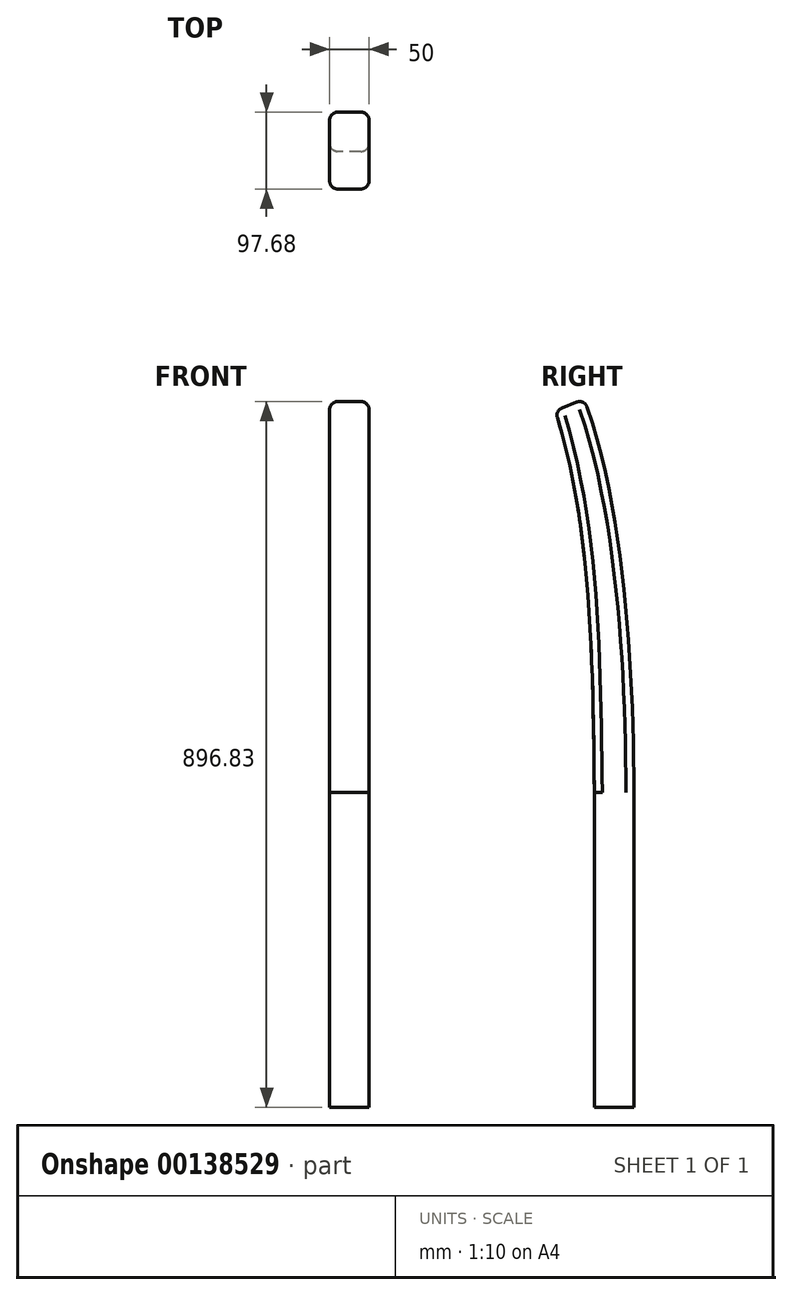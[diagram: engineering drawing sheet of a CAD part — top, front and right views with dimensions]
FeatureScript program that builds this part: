
annotation { "Feature Type Name" : "Feature", "Feature Type Description" : "" }
export const myFeature = defineFeature(function(context is Context, id is Id, definition is map)
    precondition{}
    {
        {
            var Q0;
            Q0=qCreatedBy(makeId("Right.planeOp"),FACE);
            var sketch = newSketch(context, id + "F0", { "sketchPlane" : qUnion([Q0])});
            skLineSegment(sketch, "E0.bottom", {"start": v(0, -400) * mm, "end": v(-100, -400) * mm, "construction": true});
            skLineSegment(sketch, "E0.top", {"start": v(0, 500) * mm, "end": v(-100, 500) * mm, "construction": true});
            skLineSegment(sketch, "E0.left", {"start": v(0, -400) * mm, "end": v(0, 500) * mm, "construction": true});
            skLineSegment(sketch, "E0.right", {"start": v(-100, -400) * mm, "end": v(-100, 500) * mm, "construction": true});
            skLineSegment(sketch, "E1", {"start": v(-50, -400) * mm, "end": v(-50, 0) * mm});
            skFitSpline(sketch, "E2", {"points": [v(0, 0) * mm, v(-62.92, 500) * mm], "startDerivative": vector(0, 501.4) * mm, "endDerivative": vector(-147.21, 397.99) * mm});
            skLineSegment(sketch, "E3", {"start": v(-62.92, 500) * mm, "end": v(-100, 485) * mm});
            skFitSpline(sketch, "E4", {"points": [v(-50, 0) * mm, v(-100, 485) * mm], "startDerivative": vector(-6.13, 505.96) * mm, "endDerivative": vector(-139.6, 432.37) * mm});
            skLineSegment(sketch, "E5", {"start": v(0, 0) * mm, "end": v(0, -400) * mm});
            skLineSegment(sketch, "E6", {"start": v(-50, -400) * mm, "end": v(0, -400) * mm});
            skSolve(sketch);
        }
        {
            var Q0;
            Q0=makeQuery(id+"F0.imprint","IMPRINT",FACE,{"disambiguationData":[TD([[makeQuery(id+"F0.imprint","IMPRINT",EDGE,{"derivedFrom":sQuery(id+"F0.wireOp",EDGE,"E1")}),-1.0]])]});
            extrude(context, id + "F1", {"entities" : qUnion([Q0]), "endBound" : BoundingType.SYMMETRIC, "depth" : 50 * mm});
        }
        {
            var Q0;
            Q0=makeQuery(id+"F1.opExtrude","CAP_EDGE",EDGE,{"disambiguationData":[OSD([sQuery(id+"F0.wireOp",EDGE,"E2")])],"isStart":false});
            var Q1;
            Q1=makeQuery(id+"F1.opExtrude","CAP_EDGE",EDGE,{"disambiguationData":[OSD([sQuery(id+"F0.wireOp",EDGE,"E4")])],"isStart":false});
            var Q2;
            Q2=makeQuery(id+"F1.opExtrude","CAP_EDGE",EDGE,{"disambiguationData":[OSD([sQuery(id+"F0.wireOp",EDGE,"E4")])],"isStart":true});
            var Q3;
            Q3=makeQuery(id+"F1.opExtrude","CAP_EDGE",EDGE,{"disambiguationData":[OSD([sQuery(id+"F0.wireOp",EDGE,"E2")])],"isStart":true});
            var Q4;
            Q4=makeQuery(id+"F1.opExtrude","CAP_EDGE",EDGE,{"disambiguationData":[OSD([sQuery(id+"F0.wireOp",EDGE,"E5")])],"isStart":true});
            var Q5;
            Q5=makeQuery(id+"F1.opExtrude","CAP_EDGE",EDGE,{"disambiguationData":[OSD([sQuery(id+"F0.wireOp",EDGE,"E1")])],"isStart":true});
            var Q6;
            Q6=makeQuery(id+"F1.opExtrude","CAP_EDGE",EDGE,{"disambiguationData":[OSD([sQuery(id+"F0.wireOp",EDGE,"E1")])],"isStart":false});
            var Q7;
            Q7=makeQuery(id+"F1.opExtrude","CAP_EDGE",EDGE,{"disambiguationData":[OSD([sQuery(id+"F0.wireOp",EDGE,"E5")])],"isStart":false});
            var Q8;
            Q8=makeQuery(id+"F1.opExtrude","CAP_EDGE",EDGE,{"disambiguationData":[OSD([sQuery(id+"F0.wireOp",EDGE,"E3")])],"isStart":true});
            var Q9;
            Q9=makeQuery(id+"F1.opExtrude","SWEPT_EDGE",EDGE,{"disambiguationData":[OSD([sQuery(id+"F0.wireOp",EDGE,"E3"),sQuery(id+"F0.wireOp",EDGE,"E4")])]});
            var Q10;
            Q10=makeQuery(id+"F1.opExtrude","CAP_EDGE",EDGE,{"disambiguationData":[OSD([sQuery(id+"F0.wireOp",EDGE,"E3")])],"isStart":false});
            var Q11;
            Q11=makeQuery(id+"F1.opExtrude","SWEPT_EDGE",EDGE,{"disambiguationData":[OSD([sQuery(id+"F0.wireOp",EDGE,"E2"),sQuery(id+"F0.wireOp",EDGE,"E3")])]});
            fillet(context, id + "F2", {"entities" : qUnion([Q0, Q1, Q2, Q3, Q4, Q5, Q6, Q7, Q8, Q9, Q10, Q11]), "radius" : 10 * mm, "tangentPropagation" : true, "allowEdgeOverflow" : false});
        }
    });
